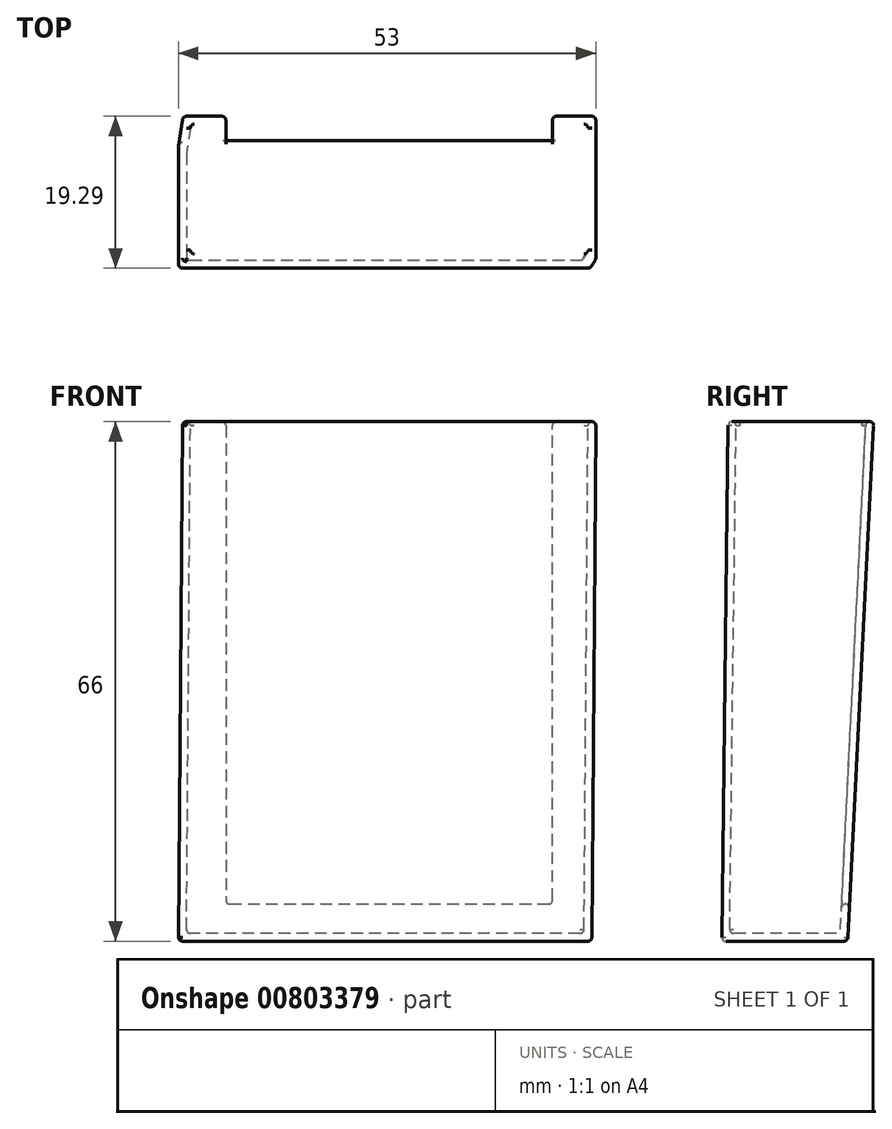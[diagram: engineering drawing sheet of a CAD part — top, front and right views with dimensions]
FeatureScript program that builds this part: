
annotation { "Feature Type Name" : "Feature", "Feature Type Description" : "" }
export const myFeature = defineFeature(function(context is Context, id is Id, definition is map)
    precondition{}
    {
        {
            var Q0;
            Q0=qCreatedBy(makeId("Top.planeOp"),FACE);
            var sketch = newSketch(context, id + "F0", { "sketchPlane" : qUnion([Q0])});
            skLineSegment(sketch, "E0.0", {"start": v(52, 15.17) * mm, "end": v(-0.5, 15.17) * mm});
            skLineSegment(sketch, "E0.1", {"start": v(52, -0.83) * mm, "end": v(52, 15.17) * mm});
            skLineSegment(sketch, "E0.2", {"start": v(-0.5, -0.83) * mm, "end": v(52, -0.83) * mm});
            skLineSegment(sketch, "E0.3", {"start": v(-0.5, 15.17) * mm, "end": v(-0.5, -0.83) * mm});
            skSolve(sketch);
        }
        {
            var Q0;
            Q0=qCreatedBy(makeId("Top.planeOp"),FACE);
            cPlane(context, id + "F1", {"entities" : qUnion([Q0]), "cplaneType" : CPlaneType.OFFSET, "offset" : 66 * mm, "width" : 150 * mm, "height" : 150 * mm});
        }
        {
            var Q0;
            Q0=qCreatedBy(id+"F1.planeOp",FACE);
            var sketch = newSketch(context, id + "F2", { "sketchPlane" : qUnion([Q0])});
            skLineSegment(sketch, "E1", {"start": v(0, 0) * mm, "end": v(52.5, 0) * mm});
            skLineSegment(sketch, "E2", {"start": v(52.5, 0) * mm, "end": v(52.5, 18.5) * mm});
            skLineSegment(sketch, "E3", {"start": v(52.5, 18.5) * mm, "end": v(0, 18.5) * mm});
            skLineSegment(sketch, "E4", {"start": v(0, 18.5) * mm, "end": v(0, 0) * mm});
            skSolve(sketch);
        }
        {
            var Q0;
            Q0=makeQuery(id+"F0.imprint","IMPRINT",FACE,{"disambiguationData":[TD([[makeQuery(id+"F0.imprint","IMPRINT",EDGE,{"derivedFrom":sQuery(id+"F0.wireOp",EDGE,"E0.0")}),1.0]])]});
            var Q1;
            Q1=makeQuery(id+"F2.imprint","IMPRINT",FACE,{"disambiguationData":[TD([[makeQuery(id+"F2.imprint","IMPRINT",EDGE,{"derivedFrom":sQuery(id+"F2.wireOp",EDGE,"E1")}),1.0]])]});
            loft(context, id + "F3", {"sheetProfilesArray" : [{ "sheetProfileEntities" : qUnion([Q0]) }, { "sheetProfileEntities" : qUnion([Q1]) }]});
        }
        {
            var Q0;
            Q0=makeQuery(id+"F3.opLoft","CAP_FACE",FACE,{"disambiguationData":[OSD([makeQuery(id+"F2.imprint","IMPRINT",FACE,{"disambiguationData":[TD([[makeQuery(id+"F2.imprint","IMPRINT",EDGE,{"derivedFrom":sQuery(id+"F2.wireOp",EDGE,"E1")}),1.0]])]})])],"isStart":true});
            shell(context, id + "F4", {"entities" : qUnion([Q0]), "thickness" : 1 * mm});
        }
        {
            var Q0;
            Q0=makeQuery(id+"F3.opLoft","SWEPT_FACE",FACE,{"disambiguationData":[OSD([sQuery(id+"F0.wireOp",EDGE,"E0.0"),sQuery(id+"F0.wireOp",EDGE,"E0.1"),sQuery(id+"F0.wireOp",EDGE,"E0.3"),sQuery(id+"F2.wireOp",EDGE,"E2"),sQuery(id+"F2.wireOp",EDGE,"E3"),sQuery(id+"F2.wireOp",EDGE,"E4")])]});
            var sketch = newSketch(context, id + "F5", { "sketchPlane" : qUnion([Q0])});
            skLineSegment(sketch, "E5", {"start": v(-52.5, 66.85) * mm, "end": v(-47, 66.85) * mm, "construction": true});
            skLineSegment(sketch, "E6", {"start": v(-47, 66.85) * mm, "end": v(-47, 5.46) * mm});
            skLineSegment(sketch, "E7", {"start": v(-47, 5.46) * mm, "end": v(-5.5, 5.46) * mm});
            skLineSegment(sketch, "E8", {"start": v(-5.5, 5.46) * mm, "end": v(-5.5, 66.85) * mm});
            skLineSegment(sketch, "E9", {"start": v(-5.5, 66.85) * mm, "end": v(0, 66.85) * mm});
            skLineSegment(sketch, "E10", {"start": v(0, 66.85) * mm, "end": v(-5.5, 66.85) * mm, "construction": true});
            skSolve(sketch);
        }
        {
            var Q0;
            {var subQ0=sQuery(id+"F5.wireOp",EDGE,"E6");Q0=makeQuery(id+"F5.imprint","IMPRINT",FACE,{"disambiguationData":[TD([[makeQuery(id+"F5.imprint","IMPRINT",EDGE,{"derivedFrom":subQ0}),1.0]])]});}
            extrude(context, id + "F6", {"entities" : qUnion([Q0]), "operationType" : NewBodyOperationType.REMOVE, "oppositeDirection" : true, "depth" : 2 * mm, "offsetDistance" : 25 * mm});
        }
        {
            var Q0;
            Q0=makeQuery(id+"F3.opLoft","SWEPT_EDGE",EDGE,{"disambiguationData":[OSD([sQuery(id+"F0.wireOp",EDGE,"E0.0"),sQuery(id+"F0.wireOp",EDGE,"E0.1"),sQuery(id+"F2.wireOp",EDGE,"E2"),sQuery(id+"F2.wireOp",EDGE,"E3")])]});
            var Q1;
            Q1=makeQuery(id+"F3.opLoft","SWEPT_FACE",FACE,{"disambiguationData":[OSD([sQuery(id+"F0.wireOp",EDGE,"E0.0"),sQuery(id+"F0.wireOp",EDGE,"E0.2"),sQuery(id+"F0.wireOp",EDGE,"E0.3"),sQuery(id+"F2.wireOp",EDGE,"E1"),sQuery(id+"F2.wireOp",EDGE,"E3"),sQuery(id+"F2.wireOp",EDGE,"E4")])]});
            var Q2;
            Q2=makeQuery(id+"F3.opLoft","MID_CAP_EDGE",EDGE,{"disambiguationData":[OSD([sQuery(id+"F2.wireOp",EDGE,"E1"),sQuery(id+"F2.wireOp",EDGE,"E2"),sQuery(id+"F2.wireOp",EDGE,"E4")])],"capPos":1.0});
            var Q3;
            Q3=makeQuery(id+"F3.opLoft","MID_CAP_EDGE",EDGE,{"disambiguationData":[OSD([sQuery(id+"F2.wireOp",EDGE,"E1"),sQuery(id+"F2.wireOp",EDGE,"E3"),sQuery(id+"F2.wireOp",EDGE,"E4")])],"capPos":1.0});
            var Q4;
            Q4=makeQuery(id+"F3.opLoft","CAP_FACE",FACE,{"disambiguationData":[OSD([makeQuery(id+"F0.imprint","IMPRINT",FACE,{"disambiguationData":[TD([[makeQuery(id+"F0.imprint","IMPRINT",EDGE,{"derivedFrom":sQuery(id+"F0.wireOp",EDGE,"E0.0")}),1.0]])]})])],"isStart":true});
            var Q5;
            Q5=makeQuery(id+"F4.opShell","OFFSET_FACE",FACE,{"disambiguationData":[OSD([sQuery(id+"F0.wireOp",EDGE,"E0.0"),sQuery(id+"F0.wireOp",EDGE,"E0.1"),sQuery(id+"F0.wireOp",EDGE,"E0.2"),sQuery(id+"F2.wireOp",EDGE,"E1"),sQuery(id+"F2.wireOp",EDGE,"E2"),sQuery(id+"F2.wireOp",EDGE,"E3")])]});
            var Q6;
            Q6=makeQuery(id+"F4.opShell","OFFSET_FACE",FACE,{"disambiguationData":[OSD([sQuery(id+"F0.wireOp",EDGE,"E0.0"),sQuery(id+"F0.wireOp",EDGE,"E0.2"),sQuery(id+"F0.wireOp",EDGE,"E0.3"),sQuery(id+"F2.wireOp",EDGE,"E1"),sQuery(id+"F2.wireOp",EDGE,"E3"),sQuery(id+"F2.wireOp",EDGE,"E4")])]});
            var Q7;
            Q7=makeQuery(id+"F4.opShell","OFFSET_FACE",FACE,{"disambiguationData":[OSD([sQuery(id+"F0.wireOp",EDGE,"E0.1"),sQuery(id+"F0.wireOp",EDGE,"E0.2"),sQuery(id+"F0.wireOp",EDGE,"E0.3"),sQuery(id+"F2.wireOp",EDGE,"E1"),sQuery(id+"F2.wireOp",EDGE,"E2"),sQuery(id+"F2.wireOp",EDGE,"E4")])]});
            var Q8;
            Q8=makeQuery(id+"F4.opShell","OFFSET_EDGE",EDGE,{"disambiguationData":[OSD([sQuery(id+"F2.wireOp",EDGE,"E1"),sQuery(id+"F2.wireOp",EDGE,"E2"),sQuery(id+"F2.wireOp",EDGE,"E4")])]});
            var Q9;
            Q9=makeQuery(id+"F6.boolean.opBoolean","COPY",FACE,{"derivedFrom":makeQuery(id+"F6.opExtrude","SWEPT_FACE",FACE,{"disambiguationData":[OSD([sQuery(id+"F5.wireOp",EDGE,"E7")])]})});
            var Q10;
            Q10=makeQuery(id+"F6.boolean.opBoolean","COPY",EDGE,{"derivedFrom":makeQuery(id+"F6.opExtrude","CAP_EDGE",EDGE,{"disambiguationData":[OSD([sQuery(id+"F5.wireOp",EDGE,"E6")])],"isStart":true})});
            var Q11;
            Q11=makeQuery(id+"F6.boolean.opBoolean","COPY",EDGE,{"derivedFrom":makeQuery(id+"F6.opExtrude","CAP_EDGE",EDGE,{"disambiguationData":[OSD([sQuery(id+"F5.wireOp",EDGE,"E7")])],"isStart":true})});
            var Q12;
            Q12=makeQuery(id+"F3.opLoft","SWEPT_FACE",FACE,{"disambiguationData":[OSD([sQuery(id+"F0.wireOp",EDGE,"E0.0"),sQuery(id+"F0.wireOp",EDGE,"E0.1"),sQuery(id+"F0.wireOp",EDGE,"E0.3"),sQuery(id+"F2.wireOp",EDGE,"E2"),sQuery(id+"F2.wireOp",EDGE,"E3"),sQuery(id+"F2.wireOp",EDGE,"E4")])]});
            var Q13;
            Q13=makeQuery(id+"F3.opLoft","CAP_FACE",FACE,{"disambiguationData":[OSD([makeQuery(id+"F2.imprint","IMPRINT",FACE,{"disambiguationData":[TD([[makeQuery(id+"F2.imprint","IMPRINT",EDGE,{"derivedFrom":sQuery(id+"F2.wireOp",EDGE,"E1")}),1.0]])]})])],"isStart":true});
            var Q14;
            Q14=makeQuery(id+"F6.boolean.opBoolean","INTERSECT",EDGE,{"derivedFrom":[makeQuery(id+"F4.opShell","OFFSET_FACE",FACE,{"disambiguationData":[OSD([sQuery(id+"F0.wireOp",EDGE,"E0.0"),sQuery(id+"F0.wireOp",EDGE,"E0.1"),sQuery(id+"F0.wireOp",EDGE,"E0.3"),sQuery(id+"F2.wireOp",EDGE,"E2"),sQuery(id+"F2.wireOp",EDGE,"E3"),sQuery(id+"F2.wireOp",EDGE,"E4")])]}),makeQuery(id+"F6.opExtrude","SWEPT_FACE",FACE,{"disambiguationData":[OSD([sQuery(id+"F5.wireOp",EDGE,"E7")])]})]});
            var Q15;
            Q15=makeQuery(id+"F3.opLoft","SWEPT_FACE",FACE,{"disambiguationData":[OSD([sQuery(id+"F0.wireOp",EDGE,"E0.0"),sQuery(id+"F0.wireOp",EDGE,"E0.1"),sQuery(id+"F0.wireOp",EDGE,"E0.2"),sQuery(id+"F2.wireOp",EDGE,"E1"),sQuery(id+"F2.wireOp",EDGE,"E2"),sQuery(id+"F2.wireOp",EDGE,"E3")])]});
            var Q16;
            Q16=makeQuery(id+"F3.opLoft","MID_CAP_EDGE",EDGE,{"disambiguationData":[OSD([sQuery(id+"F0.wireOp",EDGE,"E0.0"),sQuery(id+"F0.wireOp",EDGE,"E0.1"),sQuery(id+"F0.wireOp",EDGE,"E0.2")])],"capPos":0.0});
            var Q17;
            Q17=makeQuery(id+"F3.opLoft","MID_CAP_EDGE",EDGE,{"disambiguationData":[OSD([sQuery(id+"F2.wireOp",EDGE,"E1"),sQuery(id+"F2.wireOp",EDGE,"E2"),sQuery(id+"F2.wireOp",EDGE,"E3")])],"capPos":1.0});
            var Q18;
            Q18=makeQuery(id+"F3.opLoft","SWEPT_EDGE",EDGE,{"disambiguationData":[OSD([sQuery(id+"F0.wireOp",EDGE,"E0.0"),sQuery(id+"F0.wireOp",EDGE,"E0.3"),sQuery(id+"F2.wireOp",EDGE,"E3"),sQuery(id+"F2.wireOp",EDGE,"E4")])]});
            var Q19;
            Q19=makeQuery(id+"F3.opLoft","MID_CAP_EDGE",EDGE,{"disambiguationData":[OSD([sQuery(id+"F0.wireOp",EDGE,"E0.0"),sQuery(id+"F0.wireOp",EDGE,"E0.2"),sQuery(id+"F0.wireOp",EDGE,"E0.3")])],"capPos":0.0});
            var Q20;
            Q20=makeQuery(id+"F6.boolean.opBoolean","COPY",EDGE,{"derivedFrom":makeQuery(id+"F6.opExtrude","SWEPT_EDGE",EDGE,{"disambiguationData":[OSD([sQuery(id+"F5.wireOp",EDGE,"E6"),sQuery(id+"F5.wireOp",EDGE,"E7")])]})});
            var Q21;
            Q21=makeQuery(id+"F3.opLoft","MID_CAP_EDGE",EDGE,{"disambiguationData":[OSD([sQuery(id+"F0.wireOp",EDGE,"E0.0"),sQuery(id+"F0.wireOp",EDGE,"E0.1"),sQuery(id+"F0.wireOp",EDGE,"E0.3")])],"capPos":0.0});
            var Q22;
            Q22=makeQuery(id+"F3.opLoft","SWEPT_FACE",FACE,{"disambiguationData":[OSD([sQuery(id+"F0.wireOp",EDGE,"E0.1"),sQuery(id+"F0.wireOp",EDGE,"E0.2"),sQuery(id+"F0.wireOp",EDGE,"E0.3"),sQuery(id+"F2.wireOp",EDGE,"E1"),sQuery(id+"F2.wireOp",EDGE,"E2"),sQuery(id+"F2.wireOp",EDGE,"E4")])]});
            var Q23;
            Q23=makeQuery(id+"F6.boolean.opBoolean","COPY",FACE,{"derivedFrom":makeQuery(id+"F6.opExtrude","SWEPT_FACE",FACE,{"disambiguationData":[OSD([sQuery(id+"F5.wireOp",EDGE,"E6")])]})});
            var Q24;
            Q24=makeQuery(id+"F4.opShell","OFFSET_EDGE",EDGE,{"disambiguationData":[OSD([sQuery(id+"F0.wireOp",EDGE,"E0.0"),sQuery(id+"F0.wireOp",EDGE,"E0.1"),sQuery(id+"F2.wireOp",EDGE,"E2"),sQuery(id+"F2.wireOp",EDGE,"E3")])]});
            var Q25;
            Q25=makeQuery(id+"F4.opShell","OFFSET_EDGE",EDGE,{"disambiguationData":[OSD([sQuery(id+"F0.wireOp",EDGE,"E0.0"),sQuery(id+"F0.wireOp",EDGE,"E0.3"),sQuery(id+"F2.wireOp",EDGE,"E3"),sQuery(id+"F2.wireOp",EDGE,"E4")])]});
            var Q26;
            Q26=makeQuery(id+"F4.opShell","OFFSET_FACE",FACE,{"disambiguationData":[OSD([makeQuery(id+"F0.imprint","IMPRINT",FACE,{"disambiguationData":[TD([[makeQuery(id+"F0.imprint","IMPRINT",EDGE,{"derivedFrom":sQuery(id+"F0.wireOp",EDGE,"E0.0")}),1.0]])]})])]});
            var Q27;
            Q27=makeQuery(id+"F4.opShell","OFFSET_EDGE",EDGE,{"disambiguationData":[OSD([sQuery(id+"F0.wireOp",EDGE,"E0.1"),sQuery(id+"F0.wireOp",EDGE,"E0.2"),sQuery(id+"F2.wireOp",EDGE,"E1"),sQuery(id+"F2.wireOp",EDGE,"E2")])]});
            var Q28;
            Q28=makeQuery(id+"F4.opShell","OFFSET_EDGE",EDGE,{"disambiguationData":[OSD([sQuery(id+"F0.wireOp",EDGE,"E0.2"),sQuery(id+"F0.wireOp",EDGE,"E0.3"),sQuery(id+"F2.wireOp",EDGE,"E1"),sQuery(id+"F2.wireOp",EDGE,"E4")])]});
            var Q29;
            Q29=makeQuery(id+"F4.opShell","OFFSET_EDGE",EDGE,{"disambiguationData":[OSD([sQuery(id+"F2.wireOp",EDGE,"E1"),sQuery(id+"F2.wireOp",EDGE,"E3"),sQuery(id+"F2.wireOp",EDGE,"E4")])]});
            var Q30;
            Q30=makeQuery(id+"F4.opShell","OFFSET_EDGE",EDGE,{"disambiguationData":[OSD([sQuery(id+"F2.wireOp",EDGE,"E1"),sQuery(id+"F2.wireOp",EDGE,"E2"),sQuery(id+"F2.wireOp",EDGE,"E3")])]});
            var Q31;
            Q31=makeQuery(id+"F6.boolean.opBoolean","COPY",FACE,{"derivedFrom":makeQuery(id+"F6.opExtrude","SWEPT_FACE",FACE,{"disambiguationData":[OSD([sQuery(id+"F5.wireOp",EDGE,"E8")])]})});
            var Q32;
            Q32=makeQuery(id+"F6.boolean.opBoolean","COPY",EDGE,{"derivedFrom":makeQuery(id+"F6.opExtrude","CAP_EDGE",EDGE,{"disambiguationData":[OSD([sQuery(id+"F5.wireOp",EDGE,"E8")])],"isStart":true})});
            var Q33;
            Q33=makeQuery(id+"F4.opShell","OFFSET_FACE",FACE,{"disambiguationData":[OSD([sQuery(id+"F0.wireOp",EDGE,"E0.0"),sQuery(id+"F0.wireOp",EDGE,"E0.1"),sQuery(id+"F0.wireOp",EDGE,"E0.3"),sQuery(id+"F2.wireOp",EDGE,"E2"),sQuery(id+"F2.wireOp",EDGE,"E3"),sQuery(id+"F2.wireOp",EDGE,"E4")])]});
            var Q34;
            Q34=makeQuery(id+"F6.boolean.opBoolean","INTERSECT",EDGE,{"derivedFrom":[makeQuery(id+"F3.opLoft","CAP_FACE",FACE,{"disambiguationData":[OSD([makeQuery(id+"F2.imprint","IMPRINT",FACE,{"disambiguationData":[TD([[makeQuery(id+"F2.imprint","IMPRINT",EDGE,{"derivedFrom":sQuery(id+"F2.wireOp",EDGE,"E1")}),1.0]])]})])],"isStart":true}),makeQuery(id+"F6.opExtrude","SWEPT_FACE",FACE,{"disambiguationData":[OSD([sQuery(id+"F5.wireOp",EDGE,"E6")])]})]});
            var Q35;
            Q35=makeQuery(id+"F6.boolean.opBoolean","INTERSECT",EDGE,{"derivedFrom":[makeQuery(id+"F4.opShell","OFFSET_FACE",FACE,{"disambiguationData":[OSD([sQuery(id+"F0.wireOp",EDGE,"E0.0"),sQuery(id+"F0.wireOp",EDGE,"E0.1"),sQuery(id+"F0.wireOp",EDGE,"E0.3"),sQuery(id+"F2.wireOp",EDGE,"E2"),sQuery(id+"F2.wireOp",EDGE,"E3"),sQuery(id+"F2.wireOp",EDGE,"E4")])]}),makeQuery(id+"F6.opExtrude","SWEPT_FACE",FACE,{"disambiguationData":[OSD([sQuery(id+"F5.wireOp",EDGE,"E6")])]})]});
            var Q36;
            Q36=makeQuery(id+"F6.boolean.opBoolean","INTERSECT",EDGE,{"derivedFrom":[makeQuery(id+"F4.opShell","OFFSET_FACE",FACE,{"disambiguationData":[OSD([sQuery(id+"F0.wireOp",EDGE,"E0.0"),sQuery(id+"F0.wireOp",EDGE,"E0.1"),sQuery(id+"F0.wireOp",EDGE,"E0.3"),sQuery(id+"F2.wireOp",EDGE,"E2"),sQuery(id+"F2.wireOp",EDGE,"E3"),sQuery(id+"F2.wireOp",EDGE,"E4")])]}),makeQuery(id+"F6.opExtrude","SWEPT_FACE",FACE,{"disambiguationData":[OSD([sQuery(id+"F5.wireOp",EDGE,"E8")])]})]});
            var Q37;
            {var subQ0=sQuery(id+"F2.wireOp",EDGE,"E4");var subQ1=sQuery(id+"F2.wireOp",EDGE,"E3");var subQ2=sQuery(id+"F2.wireOp",EDGE,"E2");Q37=makeQuery(id+"F6.boolean.opBoolean","SPLIT",EDGE,{"disambiguationData":[TD([makeQuery(id+"F6.opExtrude","SWEPT_FACE",FACE,{"disambiguationData":[OSD([sQuery(id+"F5.wireOp",EDGE,"E6")])]})])],"derivedFrom":makeQuery(id+"F3.opLoft","MID_CAP_EDGE",EDGE,{"disambiguationData":[OSD([subQ2,subQ1,subQ0])],"capPos":1.0})});}
            var Q38;
            {var subQ0=sQuery(id+"F2.wireOp",EDGE,"E4");var subQ1=sQuery(id+"F2.wireOp",EDGE,"E3");var subQ2=sQuery(id+"F2.wireOp",EDGE,"E2");Q38=makeQuery(id+"F6.boolean.opBoolean","SPLIT",EDGE,{"disambiguationData":[TD([makeQuery(id+"F6.opExtrude","SWEPT_FACE",FACE,{"disambiguationData":[OSD([sQuery(id+"F5.wireOp",EDGE,"E8")])]})])],"derivedFrom":makeQuery(id+"F3.opLoft","MID_CAP_EDGE",EDGE,{"disambiguationData":[OSD([subQ2,subQ1,subQ0])],"capPos":1.0})});}
            var Q39;
            Q39=makeQuery(id+"F3.opLoft","SWEPT_EDGE",EDGE,{"disambiguationData":[OSD([sQuery(id+"F0.wireOp",EDGE,"E0.2"),sQuery(id+"F0.wireOp",EDGE,"E0.3"),sQuery(id+"F2.wireOp",EDGE,"E1"),sQuery(id+"F2.wireOp",EDGE,"E4")])]});
            var Q40;
            Q40=makeQuery(id+"F3.opLoft","MID_CAP_EDGE",EDGE,{"disambiguationData":[OSD([sQuery(id+"F0.wireOp",EDGE,"E0.1"),sQuery(id+"F0.wireOp",EDGE,"E0.2"),sQuery(id+"F0.wireOp",EDGE,"E0.3")])],"capPos":0.0});
            var Q41;
            Q41=makeQuery(id+"F3.opLoft","SWEPT_EDGE",EDGE,{"disambiguationData":[OSD([sQuery(id+"F0.wireOp",EDGE,"E0.1"),sQuery(id+"F0.wireOp",EDGE,"E0.2"),sQuery(id+"F2.wireOp",EDGE,"E1"),sQuery(id+"F2.wireOp",EDGE,"E2")])]});
            var Q42;
            Q42=makeQuery(id+"F4.opShell","OFFSET_EDGE",EDGE,{"disambiguationData":[OSD([sQuery(id+"F0.wireOp",EDGE,"E0.0"),sQuery(id+"F0.wireOp",EDGE,"E0.1"),sQuery(id+"F0.wireOp",EDGE,"E0.3")])]});
            var Q43;
            Q43=makeQuery(id+"F4.opShell","OFFSET_EDGE",EDGE,{"disambiguationData":[OSD([sQuery(id+"F0.wireOp",EDGE,"E0.0"),sQuery(id+"F0.wireOp",EDGE,"E0.1"),sQuery(id+"F0.wireOp",EDGE,"E0.2")])]});
            var Q44;
            Q44=makeQuery(id+"F4.opShell","OFFSET_EDGE",EDGE,{"disambiguationData":[OSD([sQuery(id+"F0.wireOp",EDGE,"E0.0"),sQuery(id+"F0.wireOp",EDGE,"E0.2"),sQuery(id+"F0.wireOp",EDGE,"E0.3")])]});
            var Q45;
            Q45=makeQuery(id+"F4.opShell","OFFSET_EDGE",EDGE,{"disambiguationData":[OSD([sQuery(id+"F0.wireOp",EDGE,"E0.1"),sQuery(id+"F0.wireOp",EDGE,"E0.2"),sQuery(id+"F0.wireOp",EDGE,"E0.3")])]});
            var Q46;
            {var subQ1=sQuery(id+"F2.wireOp",EDGE,"E2");var subQ2=sQuery(id+"F2.wireOp",EDGE,"E3");var subQ3=sQuery(id+"F2.wireOp",EDGE,"E4");Q46=makeQuery(id+"F6.boolean.opBoolean","SPLIT",EDGE,{"disambiguationData":[TD([makeQuery(id+"F6.opExtrude","SWEPT_FACE",FACE,{"disambiguationData":[OSD([sQuery(id+"F5.wireOp",EDGE,"E8")])]})])],"derivedFrom":makeQuery(id+"F4.opShell","OFFSET_EDGE",EDGE,{"disambiguationData":[OSD([subQ1,subQ2,subQ3])]})});}
            var Q47;
            Q47=makeQuery(id+"F6.boolean.opBoolean","COPY",EDGE,{"derivedFrom":makeQuery(id+"F6.opExtrude","SWEPT_EDGE",EDGE,{"disambiguationData":[OSD([sQuery(id+"F5.wireOp",EDGE,"E7"),sQuery(id+"F5.wireOp",EDGE,"E8")])]})});
            var Q48;
            Q48=makeQuery(id+"F6.boolean.opBoolean","INTERSECT",EDGE,{"derivedFrom":[makeQuery(id+"F3.opLoft","CAP_FACE",FACE,{"disambiguationData":[OSD([makeQuery(id+"F2.imprint","IMPRINT",FACE,{"disambiguationData":[TD([[makeQuery(id+"F2.imprint","IMPRINT",EDGE,{"derivedFrom":sQuery(id+"F2.wireOp",EDGE,"E1")}),1.0]])]})])],"isStart":true}),makeQuery(id+"F6.opExtrude","SWEPT_FACE",FACE,{"disambiguationData":[OSD([sQuery(id+"F5.wireOp",EDGE,"E8")])]})]});
            var Q49;
            {var subQ1=sQuery(id+"F2.wireOp",EDGE,"E2");var subQ2=sQuery(id+"F2.wireOp",EDGE,"E3");var subQ3=sQuery(id+"F2.wireOp",EDGE,"E4");Q49=makeQuery(id+"F6.boolean.opBoolean","SPLIT",EDGE,{"disambiguationData":[TD([makeQuery(id+"F6.opExtrude","SWEPT_FACE",FACE,{"disambiguationData":[OSD([sQuery(id+"F5.wireOp",EDGE,"E6")])]})])],"derivedFrom":makeQuery(id+"F4.opShell","OFFSET_EDGE",EDGE,{"disambiguationData":[OSD([subQ1,subQ2,subQ3])]})});}
            fillet(context, id + "F7", {"entities" : qUnion([Q0, Q1, Q2, Q3, Q4, Q5, Q6, Q7, Q8, Q9, Q10, Q11, Q12, Q13, Q14, Q15, Q16, Q17, Q18, Q19, Q20, Q21, Q22, Q23, Q24, Q25, Q26, Q27, Q28, Q29, Q30, Q31, Q32, Q33, Q34, Q35, Q36, Q37, Q38, Q39, Q40, Q41, Q42, Q43, Q44, Q45, Q46, Q47, Q48, Q49]), "radius" : 0.5 * mm, "tangentPropagation" : true, "allowEdgeOverflow" : false});
        }
    });
